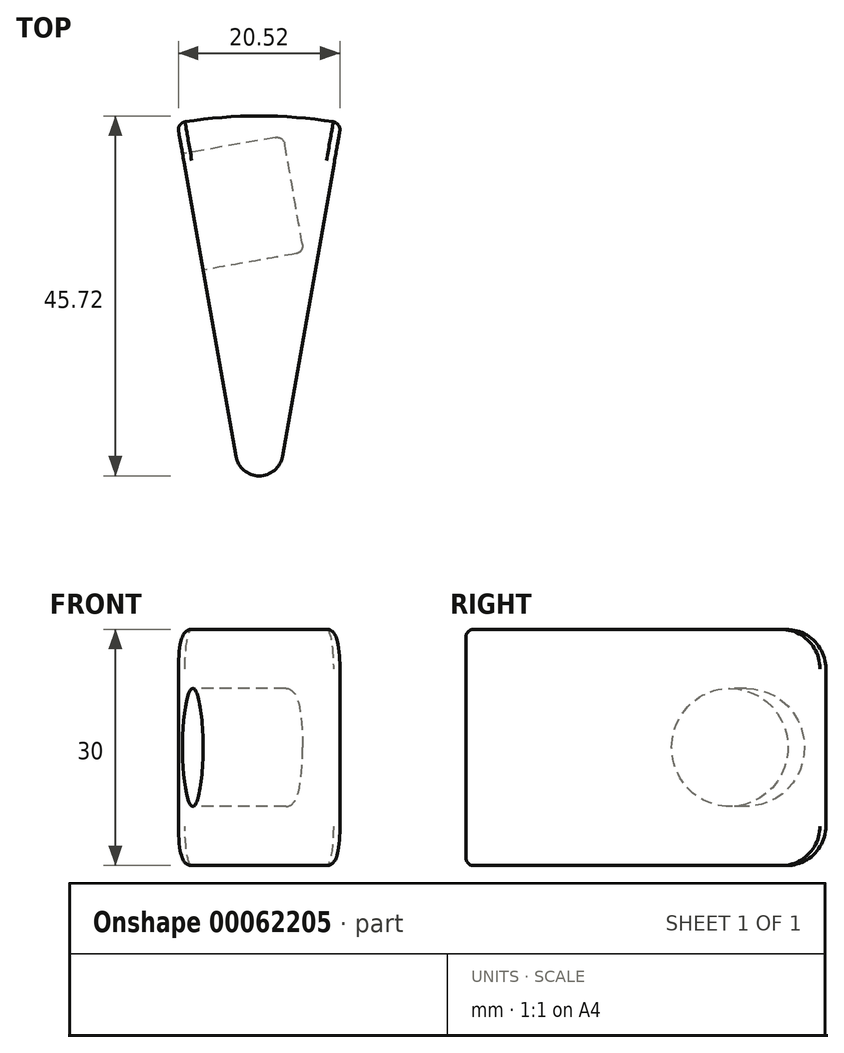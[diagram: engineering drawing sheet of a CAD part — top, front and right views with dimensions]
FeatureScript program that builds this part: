
annotation { "Feature Type Name" : "Feature", "Feature Type Description" : "" }
export const myFeature = defineFeature(function(context is Context, id is Id, definition is map)
    precondition{}
    {
        {
            var Q0;
            Q0=qCreatedBy(makeId("Right.planeOp"),FACE);
            var sketch = newSketch(context, id + "F0", { "sketchPlane" : qUnion([Q0])});
            skLineSegment(sketch, "E0.rect.bottom", {"start": v(25, 15) * mm, "end": v(-30, 15) * mm});
            skLineSegment(sketch, "E0.rect.top", {"start": v(25, -15) * mm, "end": v(-30, -15) * mm});
            skLineSegment(sketch, "E0.rect.left", {"start": v(30, 10) * mm, "end": v(30, -10) * mm});
            skPoint(sketch, "E0.rect.middle", {"position": v(0, 0) * mm});
            skPoint(sketch, "E1.visualSharp", {"position": v(30, -15) * mm});
            skArc(sketch, "E1.filletArc", {"start": v(25, -15) * mm, "mid": v(28.54, -13.54) * mm, "end": v(30, -10) * mm});
            skPoint(sketch, "E2.visualSharp", {"position": v(-30, 15) * mm});
            skPoint(sketch, "E3.visualSharp", {"position": v(30, 15) * mm});
            skArc(sketch, "E3.filletArc", {"start": v(30, 10) * mm, "mid": v(28.54, 13.54) * mm, "end": v(25, 15) * mm});
            skPoint(sketch, "E4.visualSharp", {"position": v(-30, -15) * mm});
            skLineSegment(sketch, "E5", {"start": v(-30, 15) * mm, "end": v(-30, -15) * mm});
            skSolve(sketch);
        }
        {
            var Q0;
            Q0=makeQuery(id+"F0.imprint","IMPRINT",FACE,{"disambiguationData":[TD([[makeQuery(id+"F0.imprint","IMPRINT",EDGE,{"derivedFrom":sQuery(id+"F0.wireOp",EDGE,"E0.rect.bottom")}),1.0]])]});
            var Q1;
            Q1=sQuery(id+"F0.wireOp",EDGE,"E5");
            revolve(context, id + "F1", {"entities" : qUnion([Q0]), "axis" : qUnion([Q1]), "revolveType" : RevolveType.SYMMETRIC, "angle" : 20 * degree});
        }
        {
            var Q0;
            Q0=makeQuery(id+"F1.opRevolve","CAP_EDGE",EDGE,{"disambiguationData":[OSD([sQuery(id+"F0.wireOp",EDGE,"E5")])],"isStart":true});
            fillet(context, id + "F2", {"entities" : qUnion([Q0]), "radius" : 3 * mm, "tangentPropagation" : true, "allowEdgeOverflow" : false});
        }
        {
            var Q0;
            Q0=makeQuery(id+"F1.opRevolve","CAP_FACE",FACE,{"disambiguationData":[OSD([sQuery(id+"F0.wireOp",EDGE,"E0.rect.bottom"),sQuery(id+"F0.wireOp",EDGE,"E0.rect.top"),sQuery(id+"F0.wireOp",EDGE,"E0.rect.left"),sQuery(id+"F0.wireOp",EDGE,"E1.filletArc"),sQuery(id+"F0.wireOp",EDGE,"E3.filletArc"),sQuery(id+"F0.wireOp",EDGE,"E5")])],"isStart":true});
            var sketch = newSketch(context, id + "F3", { "sketchPlane" : qUnion([Q0])});
            skCircle(sketch, "E6", {"center": v(-19, 0) * mm, "radius": 7.5 * mm});
            skSolve(sketch);
        }
        {
            var Q0;
            Q0=makeQuery(id+"F3.imprint","IMPRINT",FACE,{"disambiguationData":[TD([[makeQuery(id+"F3.imprint","IMPRINT",EDGE,{"derivedFrom":sQuery(id+"F3.wireOp",EDGE,"E6")}),1.0]])]});
            extrude(context, id + "F4", {"entities" : qUnion([Q0]), "operationType" : NewBodyOperationType.REMOVE, "oppositeDirection" : true, "depth" : 13 * mm});
        }
        {
            var Q0;
            Q0=makeQuery(id+"F1.opRevolve","CAP_EDGE",EDGE,{"disambiguationData":[OSD([sQuery(id+"F0.wireOp",EDGE,"E1.filletArc")])],"isStart":false});
            var Q1;
            Q1=makeQuery(id+"F4.boolean.opBoolean","COPY",EDGE,{"derivedFrom":makeQuery(id+"F4.opExtrude","CAP_EDGE",EDGE,{"disambiguationData":[OSD([sQuery(id+"F3.wireOp",EDGE,"E6")])],"isStart":false})});
            fillet(context, id + "F5", {"entities" : qUnion([Q0, Q1]), "radius" : 1 * mm, "tangentPropagation" : true, "allowEdgeOverflow" : false});
        }
        {
            var Q0;
            Q0=qCreatedBy(makeId("Top.planeOp"),FACE);
            var sketch = newSketch(context, id + "F6", { "sketchPlane" : qUnion([Q0])});
            skLineSegment(sketch, "E7", {"start": v(0, -30) * mm, "end": v(15, 30) * mm});
            skSolve(sketch);
        }
    });
